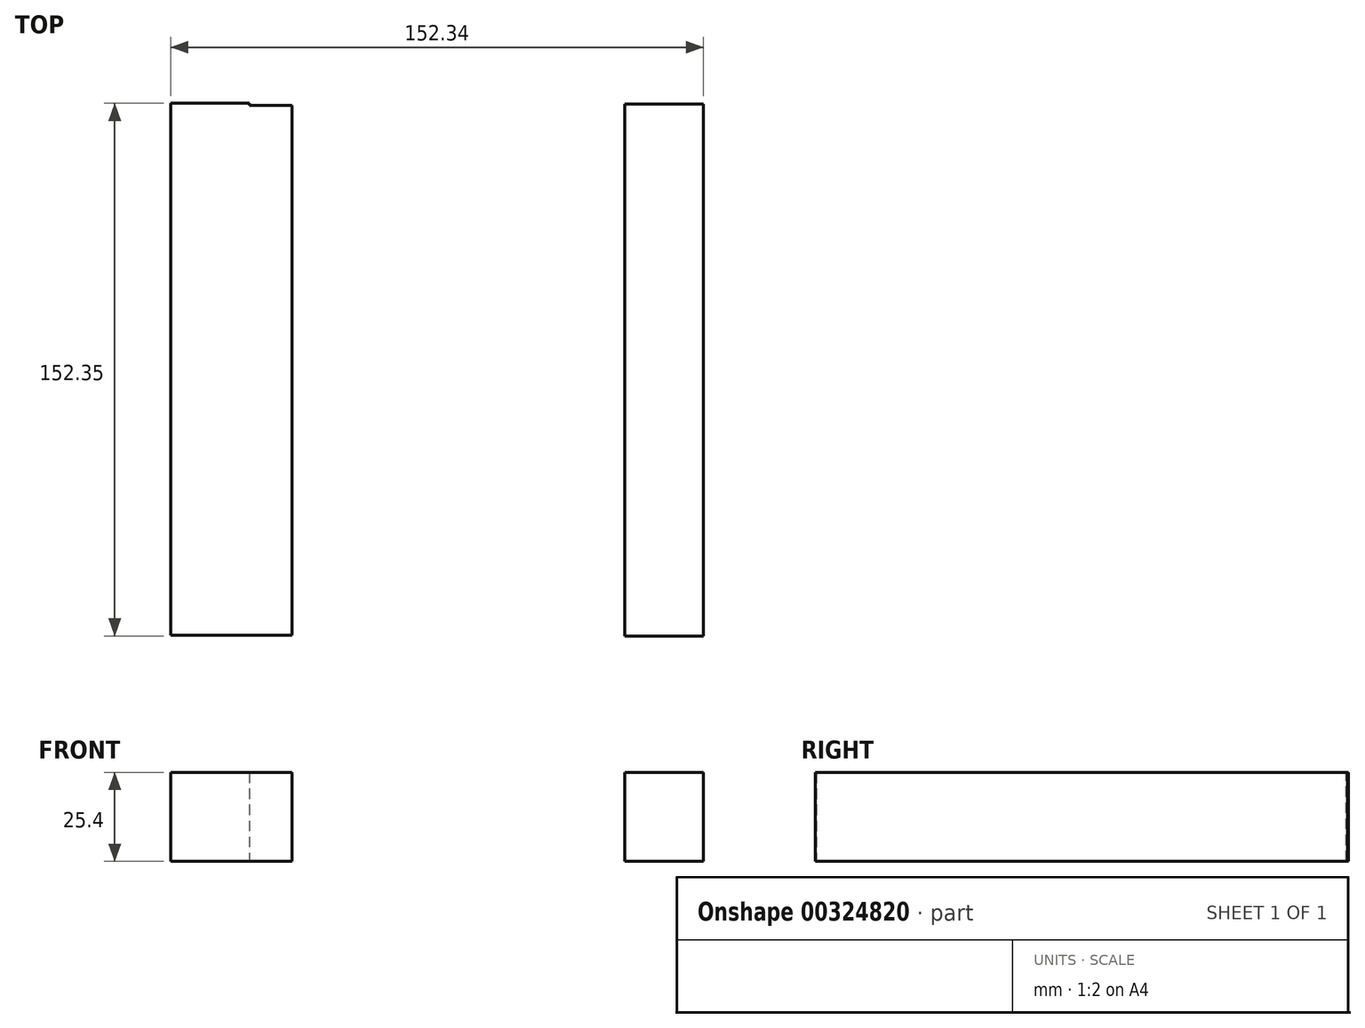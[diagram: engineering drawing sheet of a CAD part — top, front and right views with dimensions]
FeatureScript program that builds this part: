
annotation { "Feature Type Name" : "Feature", "Feature Type Description" : "" }
export const myFeature = defineFeature(function(context is Context, id is Id, definition is map)
    precondition{}
    {
        {
            var Q0;
            Q0=qCreatedBy(makeId("Top.planeOp"),FACE);
            var sketch = newSketch(context, id + "F0", { "sketchPlane" : qUnion([Q0])});
            skLineSegment(sketch, "E0.bottom", {"start": v(-76.5, 76.05) * mm, "end": v(-53.95, 76.05) * mm});
            skLineSegment(sketch, "E0.top", {"start": v(-76.5, -76.05) * mm, "end": v(-53.95, -76.05) * mm});
            skLineSegment(sketch, "E0.left", {"start": v(-76.5, 76.05) * mm, "end": v(-76.5, -76.05) * mm});
            skLineSegment(sketch, "E0.right", {"start": v(-53.95, 76.05) * mm, "end": v(-53.95, -76.05) * mm});
            skSolve(sketch);
        }
        {
            var Q0;
            Q0=makeQuery(id+"F0.imprint","IMPRINT",FACE,{"disambiguationData":[TD([[makeQuery(id+"F0.imprint","IMPRINT",EDGE,{"derivedFrom":sQuery(id+"F0.wireOp",EDGE,"E0.bottom")}),-1.0]])]});
            extrude(context, id + "F1", {"entities" : qUnion([Q0]), "depth" : 25.4 * mm});
        }
        {
            var Q0;
            Q0=makeQuery(id+"F1.opExtrude","SWEPT_BODY",BODY,{"disambiguationData":[OSD([sQuery(id+"F0.wireOp",EDGE,"E0.bottom"),sQuery(id+"F0.wireOp",EDGE,"E0.top"),sQuery(id+"F0.wireOp",EDGE,"E0.left"),sQuery(id+"F0.wireOp",EDGE,"E0.right")])]});
            transform(context, id + "F2", {"entities" : qUnion([Q0]), "transformType" : TransformType.TRANSLATION_3D, "dx" : 129.8 * mm, "dy" : -0.25 * mm, "dz" : 0 * mm, "makeCopy" : true});
        }
        {
            var Q0;
            Q0=qCreatedBy(makeId("Top.planeOp"),FACE);
            var sketch = newSketch(context, id + "F3", { "sketchPlane" : qUnion([Q0])});
            skLineSegment(sketch, "E1.bottom", {"start": v(-54.56, 75.44) * mm, "end": v(-41.76, 75.44) * mm});
            skLineSegment(sketch, "E1.top", {"start": v(-54.56, -76.05) * mm, "end": v(-41.76, -76.05) * mm});
            skLineSegment(sketch, "E1.left", {"start": v(-54.56, 75.44) * mm, "end": v(-54.56, -76.05) * mm});
            skLineSegment(sketch, "E1.right", {"start": v(-41.76, 75.44) * mm, "end": v(-41.76, -76.05) * mm});
            skSolve(sketch);
        }
        {
            var Q0;
            Q0=makeQuery(id+"F3.imprint","IMPRINT",FACE,{"disambiguationData":[TD([[makeQuery(id+"F3.imprint","IMPRINT",EDGE,{"derivedFrom":sQuery(id+"F3.wireOp",EDGE,"E1.bottom")}),-1.0]])]});
            extrude(context, id + "F4", {"entities" : qUnion([Q0]), "operationType" : NewBodyOperationType.ADD, "depth" : 25.4 * mm});
        }
    });
